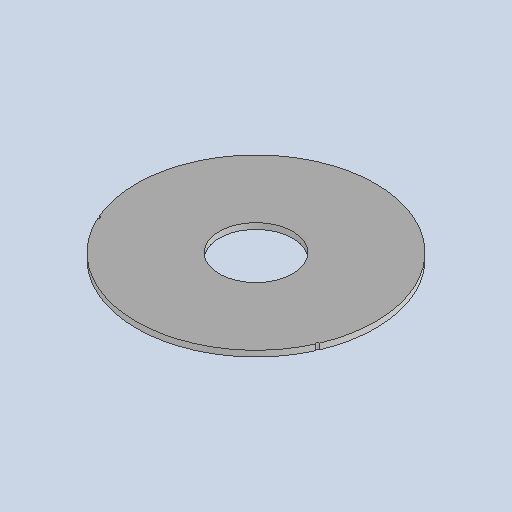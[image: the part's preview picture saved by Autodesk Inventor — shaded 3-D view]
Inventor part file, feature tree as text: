
AUTODESK INVENTOR PART (.ipt)
format: ipt  version: 2025 (Build 290162010, 162A)  size: 269,824 bytes
history: native  units: mm
features: extrude x2, other x2, sketch x2
ambient origin geometry x8: Origin, YZ Plane, XZ Plane, XY Plane, X Axis, Y Axis, Z Axis, Center Point
bodies: Solid1 (feature_tree)
feature tree (6):
  extrude  "Extrusion1"  Depth=10.0mm TaperAngle=0.0deg
  extrude  "Extrusion3"  Depth=10.0mm
  other  "A-Side Definition"
  sketch  "Sketch1"  dims[d0=390.0mm d2=10.0mm d3=0.0mm]
  sketch  "Sketch3"  dims[d4=126.0mm d13=10.0mm d14=5.0mm d15=82.5mm d16=0.0mm d17=0.0mm]
  other  "Definition1"
